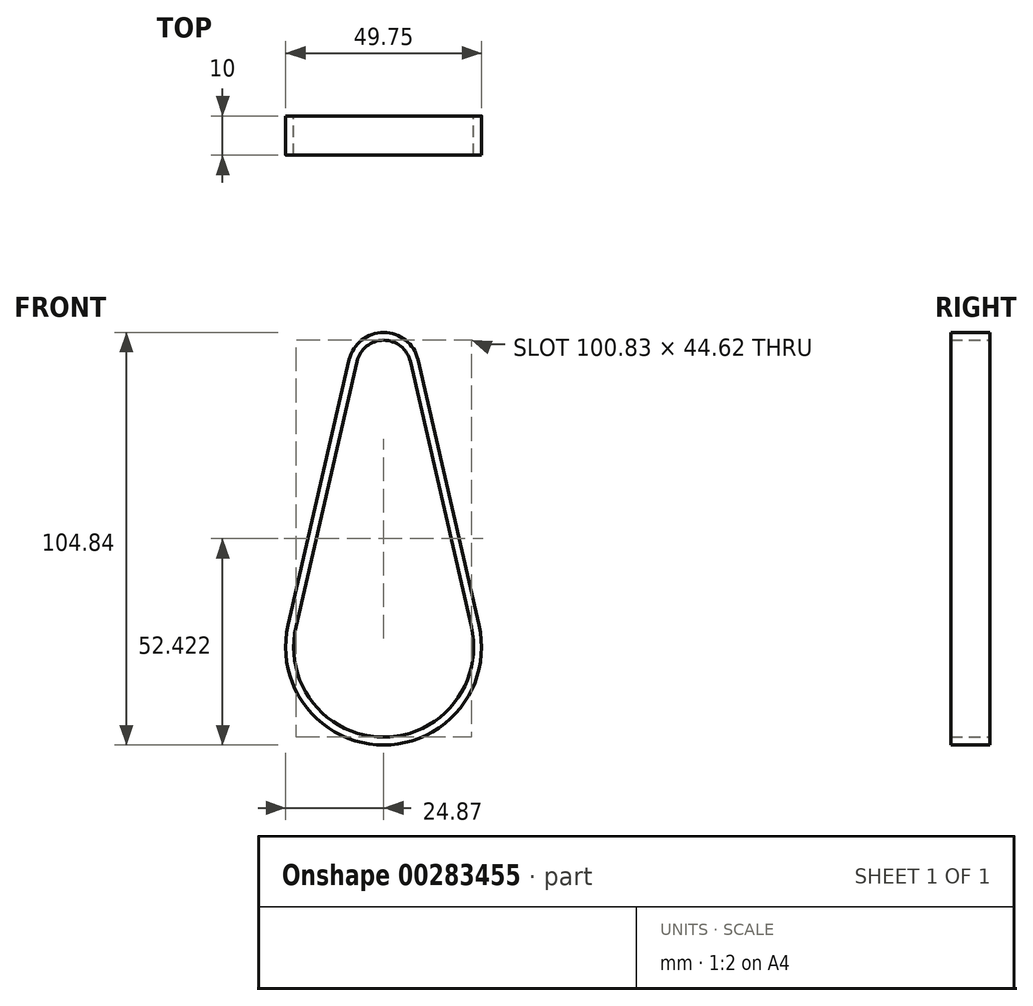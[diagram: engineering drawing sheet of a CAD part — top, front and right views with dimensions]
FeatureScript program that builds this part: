
annotation { "Feature Type Name" : "Feature", "Feature Type Description" : "" }
export const myFeature = defineFeature(function(context is Context, id is Id, definition is map)
    precondition{}
    {
        {
            var Q0;
            Q0=qCreatedBy(makeId("Front.planeOp"),FACE);
            var sketch = newSketch(context, id + "F0", { "sketchPlane" : qUnion([Q0])});
            skArc(sketch, "E0", {"start": v(-22.3, 5.13) * mm, "mid": v(0, -22.88) * mm, "end": v(22.3, 5.13) * mm});
            skArc(sketch, "E1", {"start": v(6.78, 72.56) * mm, "mid": v(0, 77.96) * mm, "end": v(-6.78, 72.56) * mm});
            skLineSegment(sketch, "E2", {"start": v(-6.78, 72.56) * mm, "end": v(-22.3, 5.13) * mm});
            skLineSegment(sketch, "E3", {"start": v(6.78, 72.56) * mm, "end": v(22.3, 5.13) * mm});
            skArc(sketch, "E4.0", {"start": v(8.73, 73) * mm, "mid": v(0, 79.96) * mm, "end": v(-8.73, 73) * mm});
            skLineSegment(sketch, "E4.1", {"start": v(8.73, 73) * mm, "end": v(24.24, 5.58) * mm});
            skArc(sketch, "E4.2", {"start": v(-24.24, 5.58) * mm, "mid": v(0, -24.88) * mm, "end": v(24.24, 5.58) * mm});
            skLineSegment(sketch, "E4.3", {"start": v(-8.73, 73) * mm, "end": v(-24.24, 5.58) * mm});
            skLineSegment(sketch, "E5.0", {"start": v(-7.76, 72.78) * mm, "end": v(-23.27, 5.35) * mm, "construction": true});
            skArc(sketch, "E5.1", {"start": v(7.76, 72.78) * mm, "mid": v(0, 78.96) * mm, "end": v(-7.76, 72.78) * mm, "construction": true});
            skLineSegment(sketch, "E5.2", {"start": v(7.76, 72.78) * mm, "end": v(23.27, 5.35) * mm, "construction": true});
            skArc(sketch, "E5.3", {"start": v(-23.27, 5.35) * mm, "mid": v(0, -23.88) * mm, "end": v(23.27, 5.35) * mm, "construction": true});
            skSolve(sketch);
        }
        {
            var Q0;
            Q0 = qSketchRegion(id + "F0", true);
            extrude(context, id + "F1", {"entities" : qUnion([Q0]), "depth" : 10 * mm});
        }
    });
